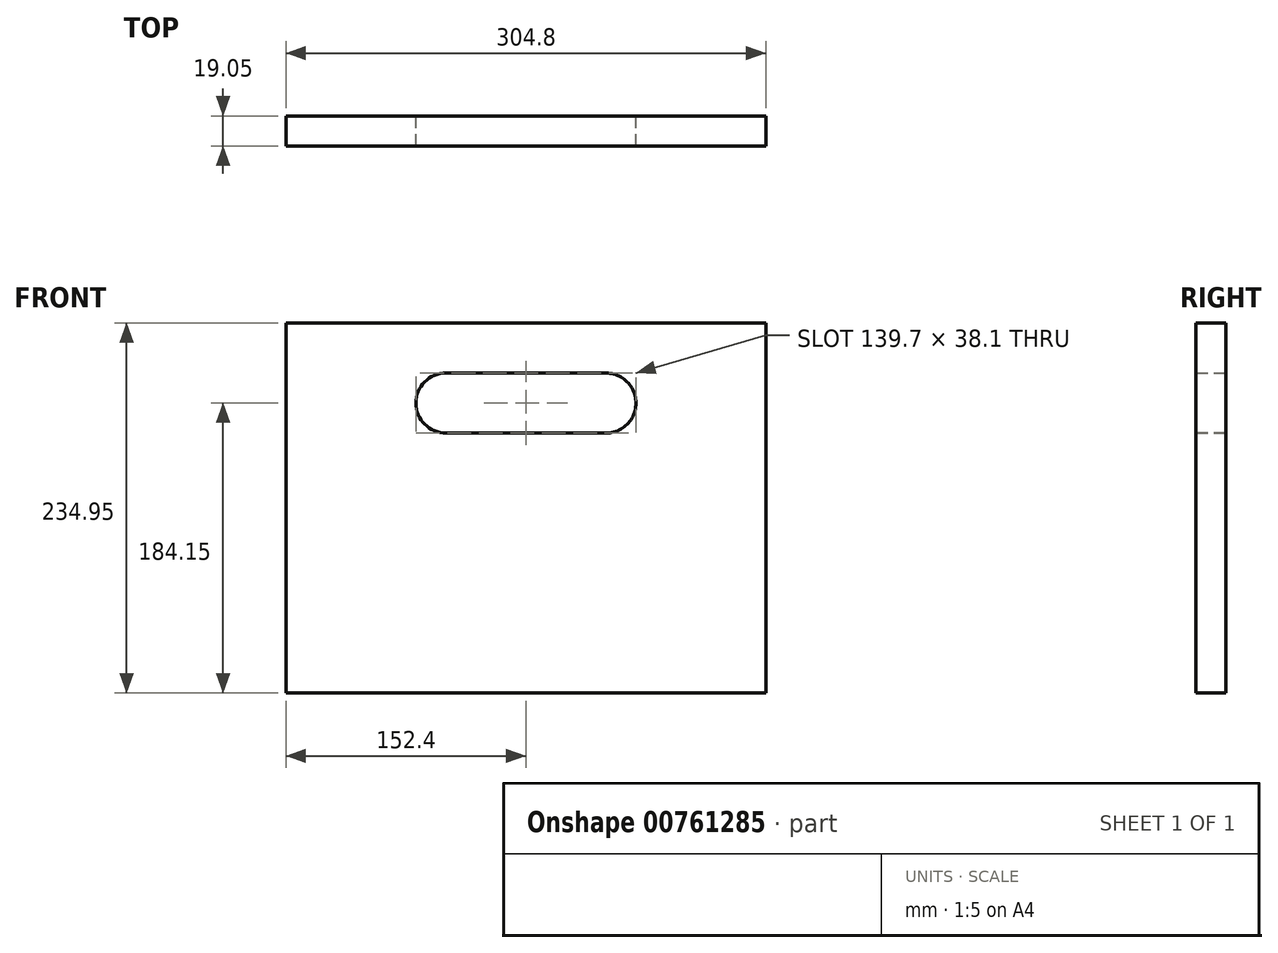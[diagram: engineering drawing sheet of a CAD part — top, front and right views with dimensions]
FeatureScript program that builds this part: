
annotation { "Feature Type Name" : "Feature", "Feature Type Description" : "" }
export const myFeature = defineFeature(function(context is Context, id is Id, definition is map)
    precondition{}
    {
        {
            var Q0;
            Q0=qCreatedBy(makeId("Front.planeOp"),FACE);
            var sketch = newSketch(context, id + "F0", { "sketchPlane" : qUnion([Q0])});
            skLineSegment(sketch, "E0.bottom", {"start": v(0, 0) * mm, "end": v(304.8, 0) * mm});
            skLineSegment(sketch, "E0.top", {"start": v(0, 234.95) * mm, "end": v(304.8, 234.95) * mm});
            skLineSegment(sketch, "E0.left", {"start": v(0, 0) * mm, "end": v(0, 234.95) * mm});
            skLineSegment(sketch, "E0.right", {"start": v(304.8, 0) * mm, "end": v(304.8, 234.95) * mm});
            skCircle(sketch, "E1", {"center": v(101.6, 184.15) * mm, "radius": 19.05 * mm});
            skCircle(sketch, "E2", {"center": v(203.2, 184.15) * mm, "radius": 19.05 * mm});
            skLineSegment(sketch, "E3", {"start": v(101.6, 203.2) * mm, "end": v(203.2, 203.2) * mm});
            skLineSegment(sketch, "E4", {"start": v(101.6, 165.1) * mm, "end": v(203.27, 165.1) * mm});
            skSolve(sketch);
        }
        {
            var Q0;
            Q0=makeQuery(id+"F0.imprint","IMPRINT",FACE,{"disambiguationData":[TD([[makeQuery(id+"F0.imprint","IMPRINT",EDGE,{"derivedFrom":sQuery(id+"F0.wireOp",EDGE,"E0.bottom")}),1.0]])]});
            extrude(context, id + "F1", {"entities" : qUnion([Q0]), "depth" : 19.05 * mm, "offsetDistance" : 25.4 * mm});
        }
    });
